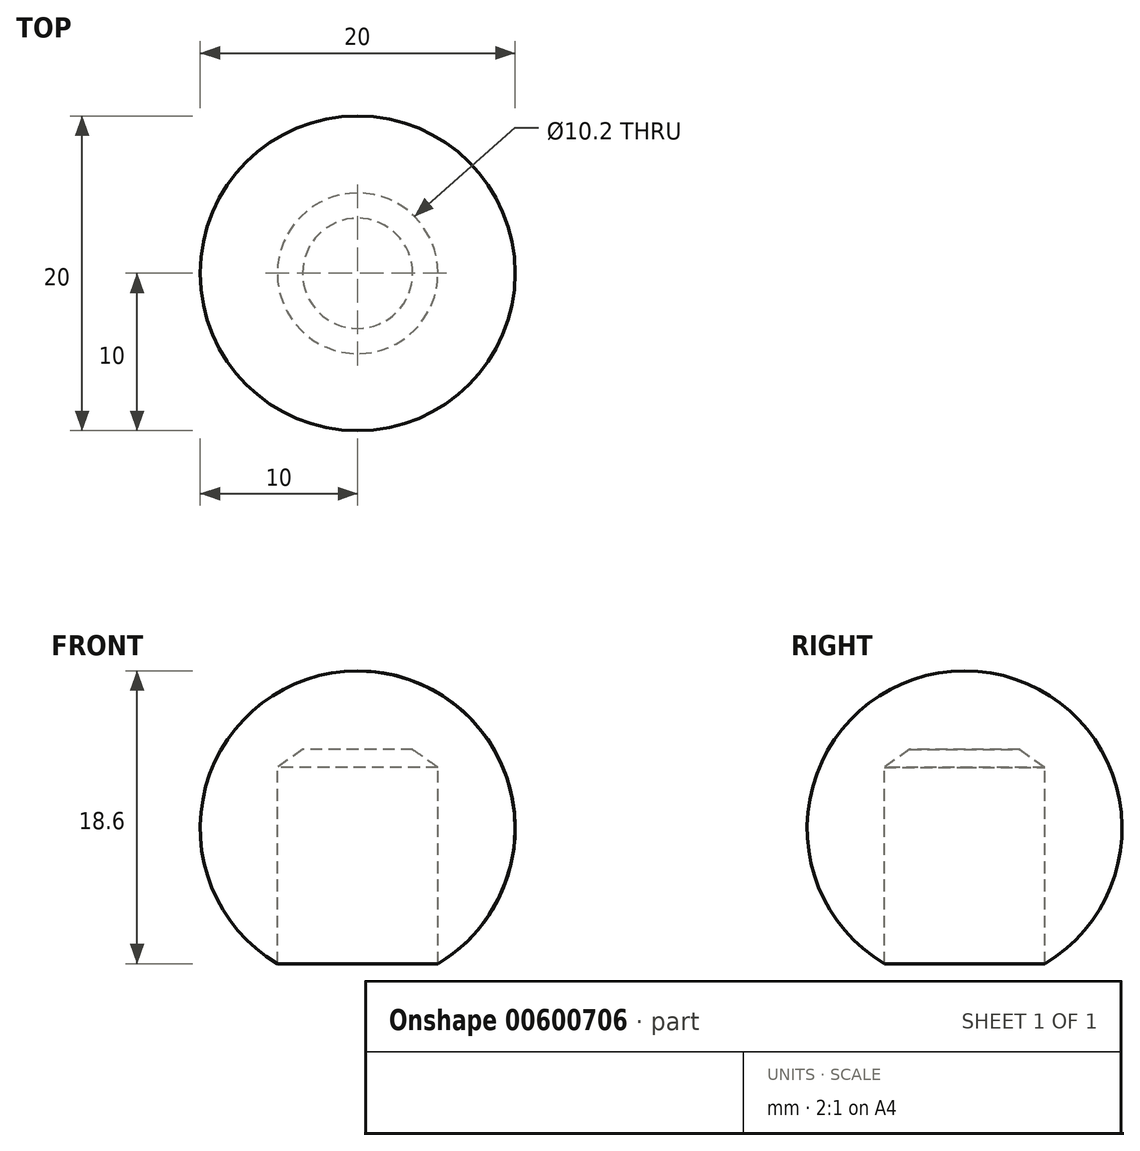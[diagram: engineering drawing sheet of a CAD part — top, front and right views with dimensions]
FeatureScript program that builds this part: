
annotation { "Feature Type Name" : "Feature", "Feature Type Description" : "" }
export const myFeature = defineFeature(function(context is Context, id is Id, definition is map)
    precondition{}
    {
        {
            var Q0;
            Q0=qCreatedBy(makeId("Front.planeOp"),FACE);
            var sketch = newSketch(context, id + "F0", { "sketchPlane" : qUnion([Q0])});
            skArc(sketch, "E0", {"start": v(5.1, -8.6) * mm, "mid": v(9.64, 2.64) * mm, "end": v(0, 10) * mm});
            skLineSegment(sketch, "E1", {"start": v(0, 10) * mm, "end": v(0, 5) * mm});
            skLineSegment(sketch, "E2", {"start": v(0, 5) * mm, "end": v(3.5, 5) * mm});
            skLineSegment(sketch, "E3", {"start": v(5.1, 3.88) * mm, "end": v(3.5, 5) * mm});
            skLineSegment(sketch, "E4", {"start": v(5.1, 3.88) * mm, "end": v(5.1, -8.6) * mm});
            skSolve(sketch);
        }
        {
            var Q0;
            Q0=makeQuery(id+"F0.imprint","IMPRINT",FACE,{"disambiguationData":[TD([[makeQuery(id+"F0.imprint","IMPRINT",EDGE,{"derivedFrom":sQuery(id+"F0.wireOp",EDGE,"E0")}),1.0]])]});
            var Q1;
            Q1=sQuery(id+"F0.wireOp",EDGE,"E1");
            revolve(context, id + "F1", {"entities" : qUnion([Q0]), "axis" : qUnion([Q1]), "revolveType" : RevolveType.FULL});
        }
    });
